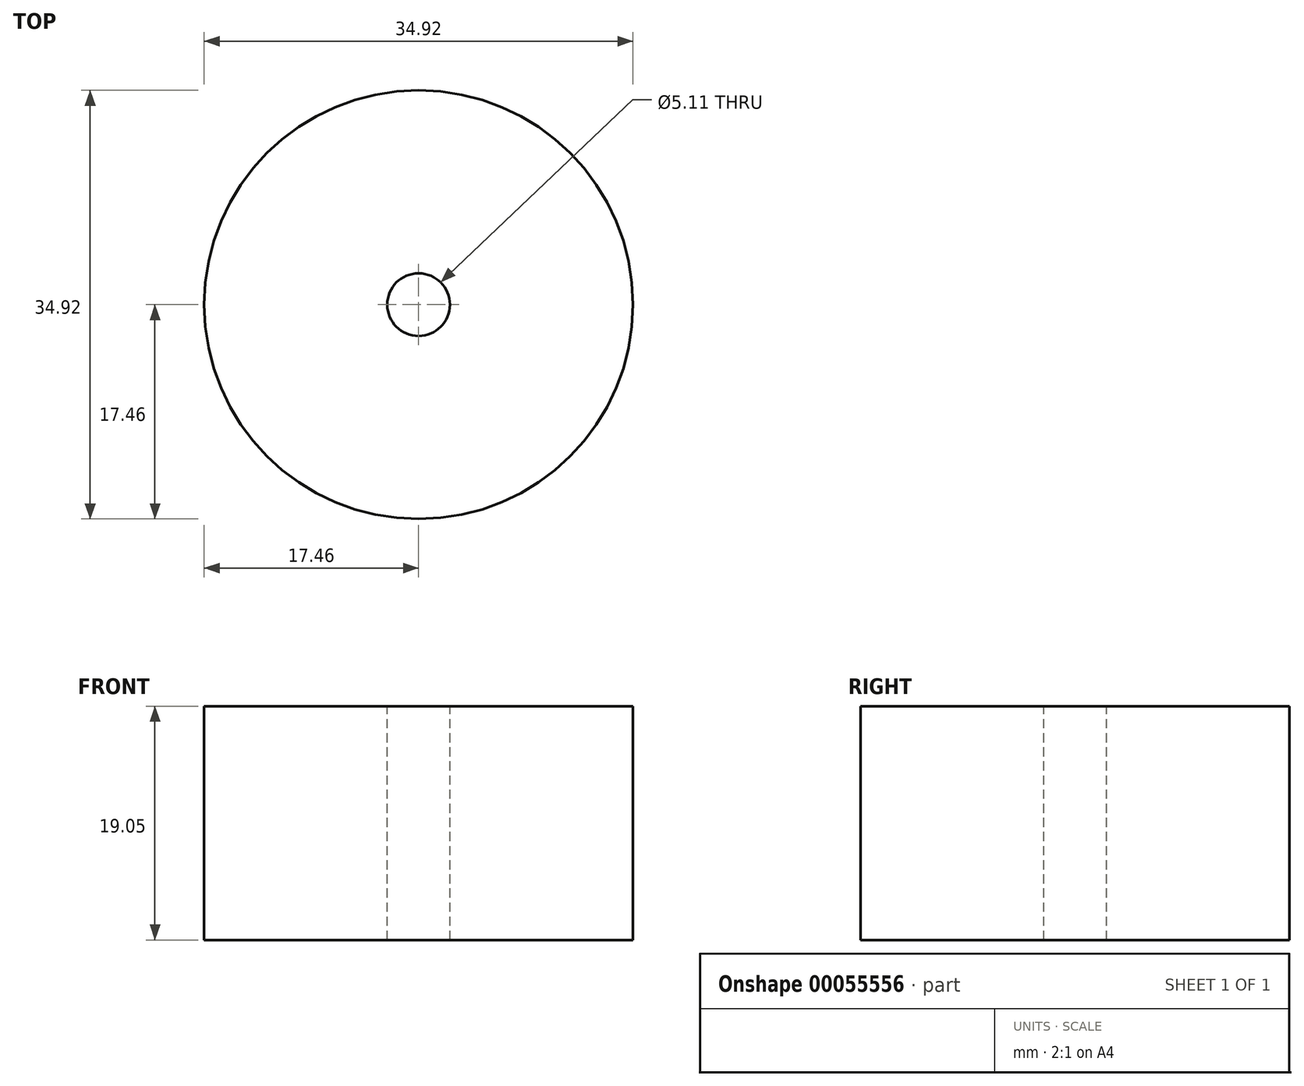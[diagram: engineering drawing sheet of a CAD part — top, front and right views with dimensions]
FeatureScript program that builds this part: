
annotation { "Feature Type Name" : "Feature", "Feature Type Description" : "" }
export const myFeature = defineFeature(function(context is Context, id is Id, definition is map)
    precondition{}
    {
        {
            var Q0;
            Q0=qCreatedBy(makeId("Top.planeOp"),FACE);
            var sketch = newSketch(context, id + "F0", { "sketchPlane" : qUnion([Q0])});
            skCircle(sketch, "E0", {"center": v(0, 0) * mm, "radius": 17.46 * mm});
            skSolve(sketch);
        }
        {
            var Q0;
            Q0=makeQuery(id+"F0.imprint","IMPRINT",FACE,{"disambiguationData":[TD([[makeQuery(id+"F0.imprint","IMPRINT",EDGE,{"derivedFrom":sQuery(id+"F0.wireOp",EDGE,"E0")}),1.0]])]});
            extrude(context, id + "F1", {"entities" : qUnion([Q0]), "depth" : 19.05 * mm});
        }
        {
            var Q0;
            Q0=makeQuery(id+"F1.opExtrude","CAP_FACE",FACE,{"disambiguationData":[OSD([sQuery(id+"F0.wireOp",EDGE,"E0")])],"isStart":false});
            var sketch = newSketch(context, id + "F2", { "sketchPlane" : qUnion([Q0])});
            skPoint(sketch, "E1", {"position": v(0, 0) * mm});
            skSolve(sketch);
        }
        {
            var Q0;
            Q0=sQuery(id+"F2.wireOp",VERTEX,"E1");
            var Q1;
            Q1=makeQuery(id+"F1.opExtrude","SWEPT_BODY",BODY,{"disambiguationData":[OSD([sQuery(id+"F0.wireOp",EDGE,"E0")])]});
            hole(context, id + "F3", {"style" : HoleStyle.SIMPLE, "endStyle" : HoleEndStyle.THROUGH, "standardTappedOrClearance" : lookupTablePath({ "standard" : "ANSI", "engagement" : "75%", "pitch" : "20 tpi", "size" : "1/4", "type" : "Tapped" }), "standardBlindInLast" : lookupTablePath({ "standard" : "ANSI", "engagement" : "75%", "pitch" : "20 tpi", "size" : "1/4", "type" : "Tapped" }), "holeDiameter" : 5.1 * mm, "locations" : qUnion([Q0]), "scope" : qUnion([Q1]), "isTappedThrough" : true, "majorDiameter" : 6.35 * mm, "showTappedDepth" : true});
        }
    });
